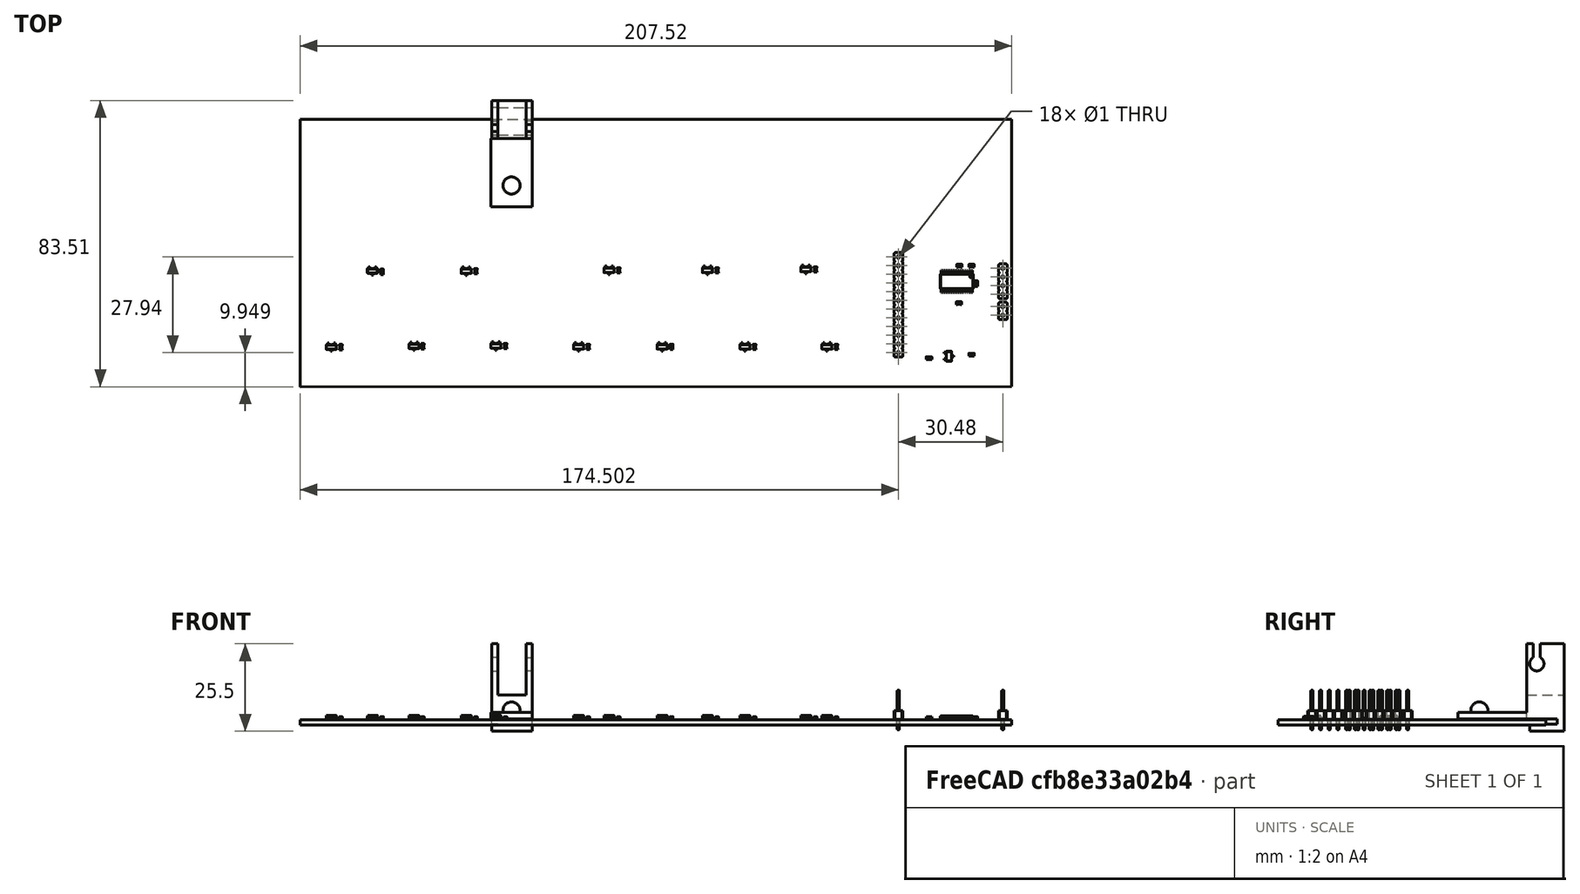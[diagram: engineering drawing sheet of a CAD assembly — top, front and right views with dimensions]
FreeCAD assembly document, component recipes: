
FREECAD ASSEMBLY — COMPONENT RECIPES ("assembly")

This assembly document has 3 components, labeled P0..P2 below (a component is one placed body or linked part). 1 of them carries a construction recipe — the FreeCAD feature program that regenerates the part from scratch, quoted from this document or its linked companion documents; the rest are supplied as boundary geometry only. No exploded tour is included for this assembly.
COMPONENT P0 — geometry summary ("Body007"; no construction recipe available for this part):
  bounding box: 76.0 x 23.5 x 3.0 mm
  tessellated surface: 96 triangles
  volume: 3653 mm^3 (68% of its bounding box)
  symmetry: mirror-symmetric across its z mid-plane
COMPONENT P1 — recipe-attached ("Body007008", modeled in this document).
Construction recipe (the document's own serialized feature program — sketch geometry with constraints, then the solid features built on it; lengths are millimeters unless a unit is written):

FEATURE [Sketcher::SketchObject] Sketch002
  FullyConstrained = true
  MapMode = 5
  Placement = pos=(0,2,0) rot=(1,0,0;1.5708rad)
  sketch-geometry (13):
    g0: LineSegment StartX=7.25 StartY=0 StartZ=0 EndX=7.25 EndY=22 EndZ=0
    g1: LineSegment StartX=-3.75 StartY=22 StartZ=0 EndX=-3.75 EndY=0 EndZ=0
    g2: LineSegment StartX=-3.75 StartY=0 StartZ=0 EndX=-3.75 EndY=-3.5 EndZ=0
    g3: LineSegment StartX=-3.75 StartY=-3.5 StartZ=0 EndX=6.25 EndY=-3.5 EndZ=0
    g4: LineSegment StartX=6.25 StartY=-3.5 StartZ=0 EndX=6.25 EndY=-1.5 EndZ=0
    g5: LineSegment StartX=6.25 StartY=-1.5 StartZ=0 EndX=-1.75 EndY=-1.5 EndZ=0
    g6: LineSegment StartX=-1.75 StartY=-1.5 StartZ=0 EndX=-1.75 EndY=0 EndZ=0
    g7: LineSegment StartX=-1.75 StartY=0 StartZ=0 EndX=7.25 EndY=0 EndZ=0
    g8: ArcOfCircle CenterX=4.25 CenterY=16.1534 CenterZ=0 NormalX=0 NormalY=0 NormalZ=1 AngleXU=0 Radius=2.1 StartAngle=2.06711 EndAngle=7.35766
    g9: LineSegment StartX=5.25 StartY=18 StartZ=0 EndX=5.25 EndY=22 EndZ=0
    g10: LineSegment StartX=5.25 StartY=22 StartZ=0 EndX=7.25 EndY=22 EndZ=0
    g11: LineSegment StartX=-3.75 StartY=22 StartZ=0 EndX=3.25 EndY=22 EndZ=0
    g12: LineSegment StartX=3.25 StartY=22 StartZ=0 EndX=3.25 EndY=18 EndZ=0
  constraints (40):
    c: Vertical(g0)
    c: PointOnObject(g1,g-1)
    c: Vertical(g1)
    c: DistanceY(g0,g0) = 22
    c: DistanceY(g1,g1) = 22
    c: DistanceX(g1,g0) = 11
    c: DistanceX(g1) = -3.75
    c: Coincident(g1,g2)
    c: Vertical(g2)
    c: Coincident(g2,g3)
    c: Horizontal(g3)
    c: Coincident(g3,g4)
    c: Vertical(g4)
    c: Coincident(g4,g5)
    c: Horizontal(g5)
    c: Coincident(g5,g6)
    c: PointOnObject(g6,g-1)
    c: Vertical(g6)
    c: Coincident(g6,g7)
    c: Coincident(g7,g0)
    c: Horizontal(g7)
    c: DistanceY(g6,g6) = 1.5
    c: DistanceY(g4,g4) = 2
    c: DistanceX(g5,g-1) = 1.75
    c: DistanceX(g3,g3) = 10
    c: Radius(g8) = 2.1
    c: Horizontal(g8,g8)
    c: DistanceX(g8,g8) = 2
    c: DistanceX(g8,g0) = 2
    c: DistanceY(g8,g0) = 4
    c: Vertical(g9)
    c: Coincident(g9,g10)
    c: Coincident(g10,g0)
    c: Horizontal(g10)
    c: Coincident(g1,g11)
    c: Horizontal(g11)
    c: Coincident(g11,g12)
    c: Coincident(g12,g8)
    c: Vertical(g12)
    c: Coincident(g9,g8)
FEATURE [PartDesign::Pad] Pad
  Direction = (0,-1,2e-16)
  Length = 1.75
  Length2 = 10
  Placement = pos=(0,2,0) rot=(1,0,0;1.5708rad)
  Profile = -> Sketch002
  ReferenceAxis = -> Sketch002 [N_Axis]
  Type = 0
FEATURE [Sketcher::SketchObject] Sketch
  FullyConstrained = true
  MapMode = 5
  Placement = pos=(0,2,0) rot=(-1,0,0;1.5708rad)
  Support = -> [Pad]
  sketch-geometry (4):
    g0: LineSegment StartX=-3.75 StartY=0 StartZ=0 EndX=7.25 EndY=0 EndZ=0
    g1: LineSegment StartX=7.25 StartY=0 StartZ=0 EndX=7.25 EndY=-7 EndZ=0
    g2: LineSegment StartX=7.25 StartY=-7 StartZ=0 EndX=-3.75 EndY=-7 EndZ=0
    g3: LineSegment StartX=-3.75 StartY=-7 StartZ=0 EndX=-3.75 EndY=0 EndZ=0
  constraints (12):
    c: Coincident(g0,g1)
    c: Coincident(g1,g2)
    c: Coincident(g2,g3)
    c: Coincident(g3,g0)
    c: Horizontal(g0)
    c: Horizontal(g2)
    c: Vertical(g1)
    c: Vertical(g3)
    c: PointOnObject(g0,g-1)
    c: DistanceX(g0,g0) = 11
    c: DistanceY(g1,g1) = 7
    c: DistanceX(g-1,g0) = 7.25
FEATURE [PartDesign::Pad] Pad001
  BaseFeature = -> Pad
  Direction = (0,1,-2e-16)
  Length = 10.5
  Length2 = 10
  Placement = pos=(0,2,0) rot=(1,0,0;1.5708rad)
  Profile = -> Sketch
  ReferenceAxis = -> Sketch [N_Axis]
  Type = 0
FEATURE [PartDesign::Plane] DatumPlane
  Length = 62.4725
  MapMode = 5
  Placement = pos=(0,12.5,-2.3e-15) rot=(-1,0,0;1.5708rad)
  ResizeMode = 0
  Support = -> [Pad001]
  Width = 60.2225
FEATURE [Sketcher::SketchObject] CopySketch003
  AttachmentOffset = pos=(0,0,0) rot=(-1,0,0;3.14159rad)
  FullyConstrained = true
  MapMode = 5
  Placement = pos=(0,12.5,-2.3e-15) rot=(-1,0,0;4.71239rad)
  Support = -> [DatumPlane]
  sketch-geometry (13):
    g0: LineSegment StartX=7.25 StartY=0 StartZ=0 EndX=7.25 EndY=22 EndZ=0
    g1: LineSegment StartX=-3.75 StartY=22 StartZ=0 EndX=-3.75 EndY=0 EndZ=0
    g2: LineSegment StartX=-3.75 StartY=0 StartZ=0 EndX=-3.75 EndY=-3.5 EndZ=0
    g3: LineSegment StartX=-3.75 StartY=-3.5 StartZ=0 EndX=6.25 EndY=-3.5 EndZ=0
    g4: LineSegment StartX=6.25 StartY=-3.5 StartZ=0 EndX=6.25 EndY=-1.5 EndZ=0
    g5: LineSegment StartX=6.25 StartY=-1.5 StartZ=0 EndX=-1.75 EndY=-1.5 EndZ=0
    g6: LineSegment StartX=-1.75 StartY=-1.5 StartZ=0 EndX=-1.75 EndY=0 EndZ=0
    g7: LineSegment StartX=-1.75 StartY=0 StartZ=0 EndX=7.25 EndY=0 EndZ=0
    g8: ArcOfCircle CenterX=4.25 CenterY=16.1534 CenterZ=0 NormalX=0 NormalY=0 NormalZ=1 AngleXU=0 Radius=2.1 StartAngle=2.06711 EndAngle=7.35766
    g9: LineSegment StartX=5.25 StartY=18 StartZ=0 EndX=5.25 EndY=22 EndZ=0
    g10: LineSegment StartX=5.25 StartY=22 StartZ=0 EndX=7.25 EndY=22 EndZ=0
    g11: LineSegment StartX=-3.75 StartY=22 StartZ=0 EndX=3.25 EndY=22 EndZ=0
    g12: LineSegment StartX=3.25 StartY=22 StartZ=0 EndX=3.25 EndY=18 EndZ=0
  constraints (40):
    c: Vertical(g0)
    c: PointOnObject(g1,g-1)
    c: Vertical(g1)
    c: DistanceY(g0,g0) = 22
    c: DistanceY(g1,g1) = 22
    c: DistanceX(g1,g0) = 11
    c: DistanceX(g1) = -3.75
    c: Coincident(g1,g2)
    c: Vertical(g2)
    c: Coincident(g2,g3)
    c: Horizontal(g3)
    c: Coincident(g3,g4)
    c: Vertical(g4)
    c: Coincident(g4,g5)
    c: Horizontal(g5)
    c: Coincident(g5,g6)
    c: PointOnObject(g6,g-1)
    c: Vertical(g6)
    c: Coincident(g6,g7)
    c: Coincident(g7,g0)
    c: Horizontal(g7)
    c: DistanceY(g6,g6) = 1.5
    c: DistanceY(g4,g4) = 2
    c: DistanceX(g5,g-1) = 1.75
    c: DistanceX(g3,g3) = 10
    c: Radius(g8) = 2.1
    c: Horizontal(g8,g8)
    c: DistanceX(g8,g8) = 2
    c: DistanceX(g8,g0) = 2
    c: DistanceY(g8,g0) = 4
    c: Vertical(g9)
    c: Coincident(g9,g10)
    c: Coincident(g10,g0)
    c: Horizontal(g10)
    c: Coincident(g1,g11)
    c: Horizontal(g11)
    c: Coincident(g11,g12)
    c: Coincident(g12,g8)
    c: Vertical(g12)
    c: Coincident(g9,g8)
FEATURE [PartDesign::Pad] Pad002
  BaseFeature = -> Pad001
  Direction = (0,1,-3e-16)
  Length = 1.75
  Length2 = 10
  Placement = pos=(0,2,0) rot=(1,0,0;1.5708rad)
  Profile = -> CopySketch003
  ReferenceAxis = -> Pad001 [Edge38]
  Type = 0
FEATURE [Sketcher::SketchObject] Sketch003
  FullyConstrained = true
  MapMode = 5
  Placement = pos=(7.25,2,0) rot=(0.707107,0,0.707107;3.14159rad)
  Support = -> [Pad002]
  sketch-geometry (4):
    g0: LineSegment StartX=0 StartY=1.75 StartZ=0 EndX=2 EndY=1.75 EndZ=0
    g1: LineSegment StartX=2 StartY=1.75 StartZ=0 EndX=2 EndY=-12.25 EndZ=0
    g2: LineSegment StartX=2 StartY=-12.25 StartZ=0 EndX=0 EndY=-12.25 EndZ=0
    g3: LineSegment StartX=0 StartY=-12.25 StartZ=0 EndX=0 EndY=1.75 EndZ=0
  constraints (12):
    c: Coincident(g0,g1)
    c: Coincident(g1,g2)
    c: Coincident(g2,g3)
    c: Coincident(g3,g0)
    c: Horizontal(g0)
    c: Horizontal(g2)
    c: Vertical(g1)
    c: Vertical(g3)
    c: PointOnObject(g0,g-2)
    c: DistanceY(g1,g1) = 14
    c: DistanceY(g-1,g0) = 1.75
    c: DistanceX(g0,g0) = 2
FEATURE [PartDesign::Pad] Pad003
  BaseFeature = -> Pad002
  Direction = (1,0,-2e-16)
  Length = 20
  Length2 = 10
  Placement = pos=(0,2,0) rot=(1,0,0;1.5708rad)
  Profile = -> Sketch003
  ReferenceAxis = -> Sketch003 [N_Axis]
  Type = 0
FEATURE [Sketcher::SketchObject] Sketch004
  FullyConstrained = true
  MapMode = 5
  Placement = pos=(4e-16,2,2) rot=(0,0,1;3.14159rad)
  Support = -> [Pad003]
  sketch-geometry (1):
    g0: Circle CenterX=-21 CenterY=-5 CenterZ=0 NormalX=0 NormalY=0 NormalZ=1 AngleXU=0 Radius=2.5
  constraints (3):
    c: Diameter(g0) = 5
    c: DistanceY(g0,g-1) = 5
    c: DistanceX(g0,g-1) = 21
FEATURE [PartDesign::Pad] Pad004
  BaseFeature = -> Pad003
  Direction = (2e-16,3e-16,1)
  Length = 3
  Length2 = 10
  Placement = pos=(0,2,0) rot=(1,0,0;1.5708rad)
  Profile = -> Sketch004
  ReferenceAxis = -> Sketch004 [N_Axis]
  Type = 0
FEATURE [PartDesign::Fillet] Fillet
  Base = -> Pad004 [Edge106]
  BaseFeature = -> Pad004
  Placement = pos=(0,2,0) rot=(1,0,0;1.5708rad)
  Radius = 2.5
  SupportTransform = false
  UseAllEdges = false
FEATURE [PartDesign::Fillet] Fillet002
  Base = -> Pad004 [Edge103]
  BaseFeature = -> Pad004
  Placement = pos=(0,2,0) rot=(1,0,0;1.5708rad)
  Radius = 2
  SupportTransform = false
  UseAllEdges = false
FEATURE [Sketcher::SketchObject] Sketch008
  FullyConstrained = true
  MapMode = 5
  Placement = pos=(0,2,0) rot=(-1,0,0;1.5708rad)
  Support = -> [Fillet]
  sketch-geometry (6):
    g0: LineSegment StartX=-3.75 StartY=0 StartZ=0 EndX=-3.75 EndY=3.5 EndZ=0
    g1: LineSegment StartX=-3.75 StartY=3.5 StartZ=0 EndX=6.25 EndY=3.5 EndZ=0
    g2: LineSegment StartX=6.25 StartY=3.5 StartZ=0 EndX=6.25 EndY=1.5 EndZ=0
    g3: LineSegment StartX=6.25 StartY=1.5 StartZ=0 EndX=-1.75 EndY=1.5 EndZ=0
    g4: LineSegment StartX=-1.75 StartY=1.5 StartZ=0 EndX=-1.75 EndY=0 EndZ=0
    g5: LineSegment StartX=-1.75 StartY=0 StartZ=0 EndX=-3.75 EndY=0 EndZ=0
  constraints (18):
    c: Vertical(g0)
    c: Coincident(g0,g1)
    c: Horizontal(g1)
    c: Coincident(g1,g2)
    c: Vertical(g2)
    c: Coincident(g2,g3)
    c: Horizontal(g3)
    c: Coincident(g3,g4)
    c: Vertical(g4)
    c: Coincident(g4,g5)
    c: Coincident(g5,g0)
    c: Horizontal(g5)
    c: DistanceX(g1,g1) = 10
    c: DistanceY(g0,g0) = 3.5
    c: DistanceY(g2,g2) = 2
    c: DistanceY(g4,g-1) = 0
    c: DistanceX(g5,g5) = 2
    c: DistanceX(g4,g-1) = 1.75
FEATURE [PartDesign::Pad] Pad008
  BaseFeature = -> Fillet
  Direction = (0,1,-7e-16)
  Length = 10
  Length2 = 10
  Placement = pos=(0,2,0) rot=(1,0,0;1.5708rad)
  Profile = -> Sketch008
  ReferenceAxis = -> Sketch008 [N_Axis]
  Type = 0
FEATURE [PartDesign::Body] Body007008
  Group = -> [Sketch002,Pad,Sketch,Pad001,CopySketch003,Pad002,Sketch003,Pad003,Sketch004,Pad004,DatumPlane,Fillet,Sketch008,Pad008,Fillet002]
  Origin = -> Origin001
  Placement = pos=(21.25,44.5,-14.25) rot=(0,0,1;4.71239rad)
  Tip = -> Fillet002
COMPONENT P2 — geometry summary ("Body008"; no construction recipe available for this part):
  bounding box: 76.0 x 23.5 x 3.0 mm
  tessellated surface: 96 triangles
  volume: 3653 mm^3 (68% of its bounding box)
  symmetry: mirror-symmetric across its z mid-plane
PROVENANCE & LICENSES
A FreeCAD (.FCStd) document from a public repository crawl; recipes are the document's own serialized feature recipes (and, for linked parts, companion documents' recipes).
License: as declared in the source repository (recorded in the dataset sidecar).
